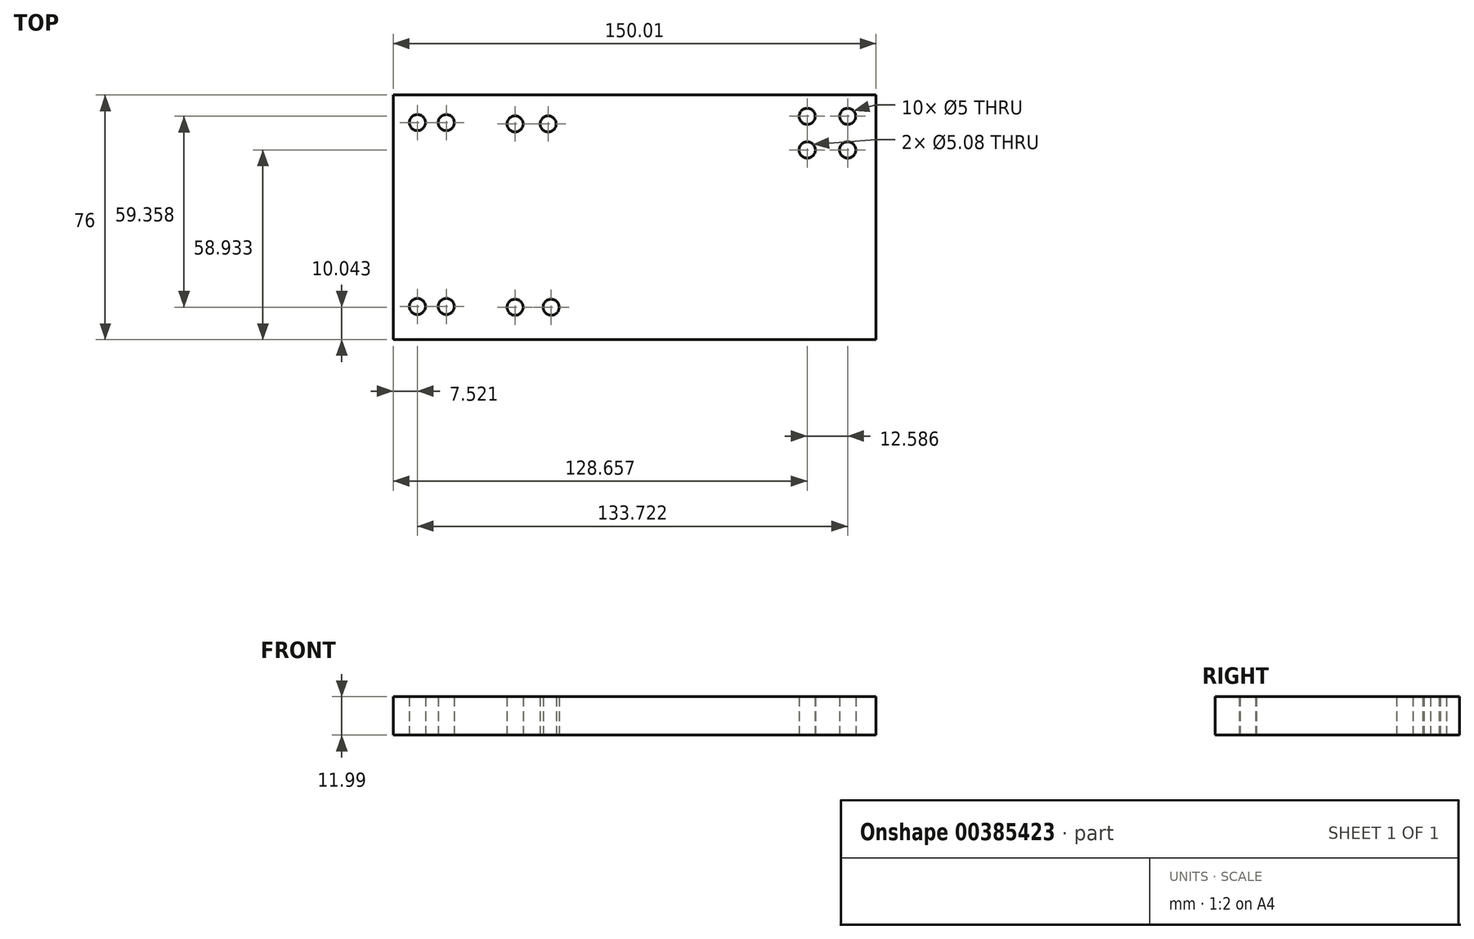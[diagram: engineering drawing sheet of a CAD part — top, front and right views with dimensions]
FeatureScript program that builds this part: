
annotation { "Feature Type Name" : "Feature", "Feature Type Description" : "" }
export const myFeature = defineFeature(function(context is Context, id is Id, definition is map)
    precondition{}
    {
        {
            var Q0;
            Q0=qCreatedBy(makeId("Top.planeOp"),FACE);
            var sketch = newSketch(context, id + "F0", { "sketchPlane" : qUnion([Q0])});
            skLineSegment(sketch, "E0", {"start": v(0, 0) * mm, "end": v(150.01, 0) * mm});
            skLineSegment(sketch, "E1", {"start": v(150.01, 0) * mm, "end": v(150.01, -76) * mm});
            skLineSegment(sketch, "E2", {"start": v(150.01, -76) * mm, "end": v(0, -76) * mm});
            skLineSegment(sketch, "E3", {"start": v(0, -76) * mm, "end": v(0, 0) * mm});
            skCircle(sketch, "E4", {"center": v(16.5, -8.55) * mm, "radius": 2.5 * mm});
            skCircle(sketch, "E5", {"center": v(7.52, -8.55) * mm, "radius": 2.5 * mm});
            skCircle(sketch, "E6", {"center": v(7.52, -65.72) * mm, "radius": 2.5 * mm});
            skCircle(sketch, "E7", {"center": v(16.5, -65.72) * mm, "radius": 2.5 * mm});
            skCircle(sketch, "E8", {"center": v(141.24, -6.6) * mm, "radius": 2.5 * mm});
            skCircle(sketch, "E9", {"center": v(141.24, -17.07) * mm, "radius": 2.54 * mm});
            skCircle(sketch, "E10", {"center": v(128.66, -6.6) * mm, "radius": 2.5 * mm});
            skCircle(sketch, "E11", {"center": v(128.66, -17.07) * mm, "radius": 2.54 * mm});
            skCircle(sketch, "E12", {"center": v(37.88, -8.97) * mm, "radius": 2.5 * mm});
            skCircle(sketch, "E13", {"center": v(48.15, -8.97) * mm, "radius": 2.5 * mm});
            skCircle(sketch, "E14", {"center": v(37.88, -65.96) * mm, "radius": 2.5 * mm});
            skCircle(sketch, "E15", {"center": v(49.09, -65.96) * mm, "radius": 2.5 * mm});
            skSolve(sketch);
        }
        {
            var Q0;
            Q0=makeQuery(id+"F0.imprint","IMPRINT",FACE,{"disambiguationData":[TD([[makeQuery(id+"F0.imprint","IMPRINT",EDGE,{"derivedFrom":sQuery(id+"F0.wireOp",EDGE,"E0")}),-1.0]])]});
            extrude(context, id + "F1", {"entities" : qUnion([Q0]), "depth" : 12 * mm});
        }
    });
